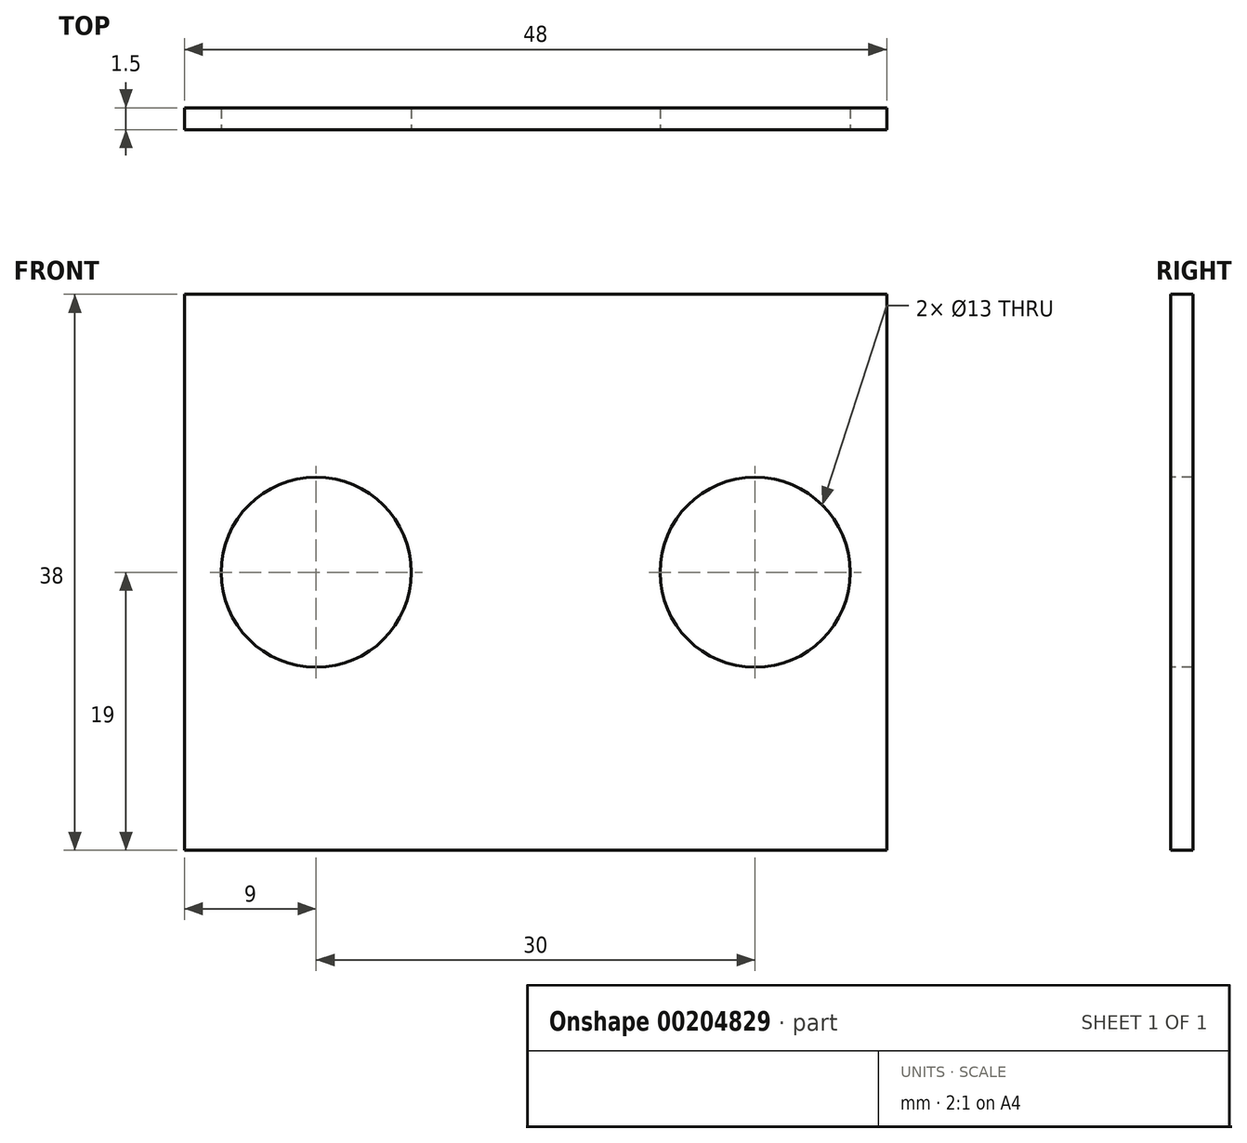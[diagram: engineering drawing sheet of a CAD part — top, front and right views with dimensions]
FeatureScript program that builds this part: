
annotation { "Feature Type Name" : "Feature", "Feature Type Description" : "" }
export const myFeature = defineFeature(function(context is Context, id is Id, definition is map)
    precondition{}
    {
        {
            var Q0;
            Q0=qCreatedBy(makeId("Front.planeOp"),FACE);
            var sketch = newSketch(context, id + "F0", { "sketchPlane" : qUnion([Q0])});
            skLineSegment(sketch, "E0.bottom", {"start": v(0, 0) * mm, "end": v(48, 0) * mm});
            skLineSegment(sketch, "E0.top", {"start": v(0, 38) * mm, "end": v(48, 38) * mm});
            skLineSegment(sketch, "E0.left", {"start": v(0, 0) * mm, "end": v(0, 38) * mm});
            skLineSegment(sketch, "E0.right", {"start": v(48, 0) * mm, "end": v(48, 38) * mm});
            skSolve(sketch);
        }
        {
            var Q0;
            Q0=makeQuery(id+"F0.imprint","IMPRINT",FACE,{"disambiguationData":[TD([[makeQuery(id+"F0.imprint","IMPRINT",EDGE,{"derivedFrom":sQuery(id+"F0.wireOp",EDGE,"E0.bottom")}),1.0]])]});
            extrude(context, id + "F1", {"entities" : qUnion([Q0]), "depth" : 1.5 * mm});
        }
        {
            var Q0;
            Q0=makeQuery(id+"F1.opExtrude","CAP_FACE",FACE,{"disambiguationData":[OSD([sQuery(id+"F0.wireOp",EDGE,"E0.bottom"),sQuery(id+"F0.wireOp",EDGE,"E0.top"),sQuery(id+"F0.wireOp",EDGE,"E0.left"),sQuery(id+"F0.wireOp",EDGE,"E0.right")])],"isStart":false});
            var sketch = newSketch(context, id + "F2", { "sketchPlane" : qUnion([Q0])});
            skCircle(sketch, "E1", {"center": v(9, 19) * mm, "radius": 6.5 * mm});
            skPoint(sketch, "E1.centerSnap0", {"position": v(0, 19) * mm});
            skCircle(sketch, "E2", {"center": v(39, 19) * mm, "radius": 6.5 * mm});
            skPoint(sketch, "E2.centerSnap0", {"position": v(48, 19) * mm});
            skSolve(sketch);
        }
        {
            var Q0;
            Q0=sQuery(id+"F2.wireOp",VERTEX,"E1.center");
            var Q1;
            Q1=sQuery(id+"F2.wireOp",VERTEX,"E2.center");
            var Q2;
            Q2=makeQuery(id+"F1.opExtrude","SWEPT_BODY",BODY,{"disambiguationData":[OSD([sQuery(id+"F0.wireOp",EDGE,"E0.bottom"),sQuery(id+"F0.wireOp",EDGE,"E0.top"),sQuery(id+"F0.wireOp",EDGE,"E0.left"),sQuery(id+"F0.wireOp",EDGE,"E0.right")])]});
            hole(context, id + "F3", {"style" : HoleStyle.SIMPLE, "endStyle" : HoleEndStyle.BLIND, "holeDiameter" : 13 * mm, "holeDepth" : 10 * mm, "startFromSketch" : true, "locations" : qUnion([Q0, Q1]), "scope" : qUnion([Q2])});
        }
    });
